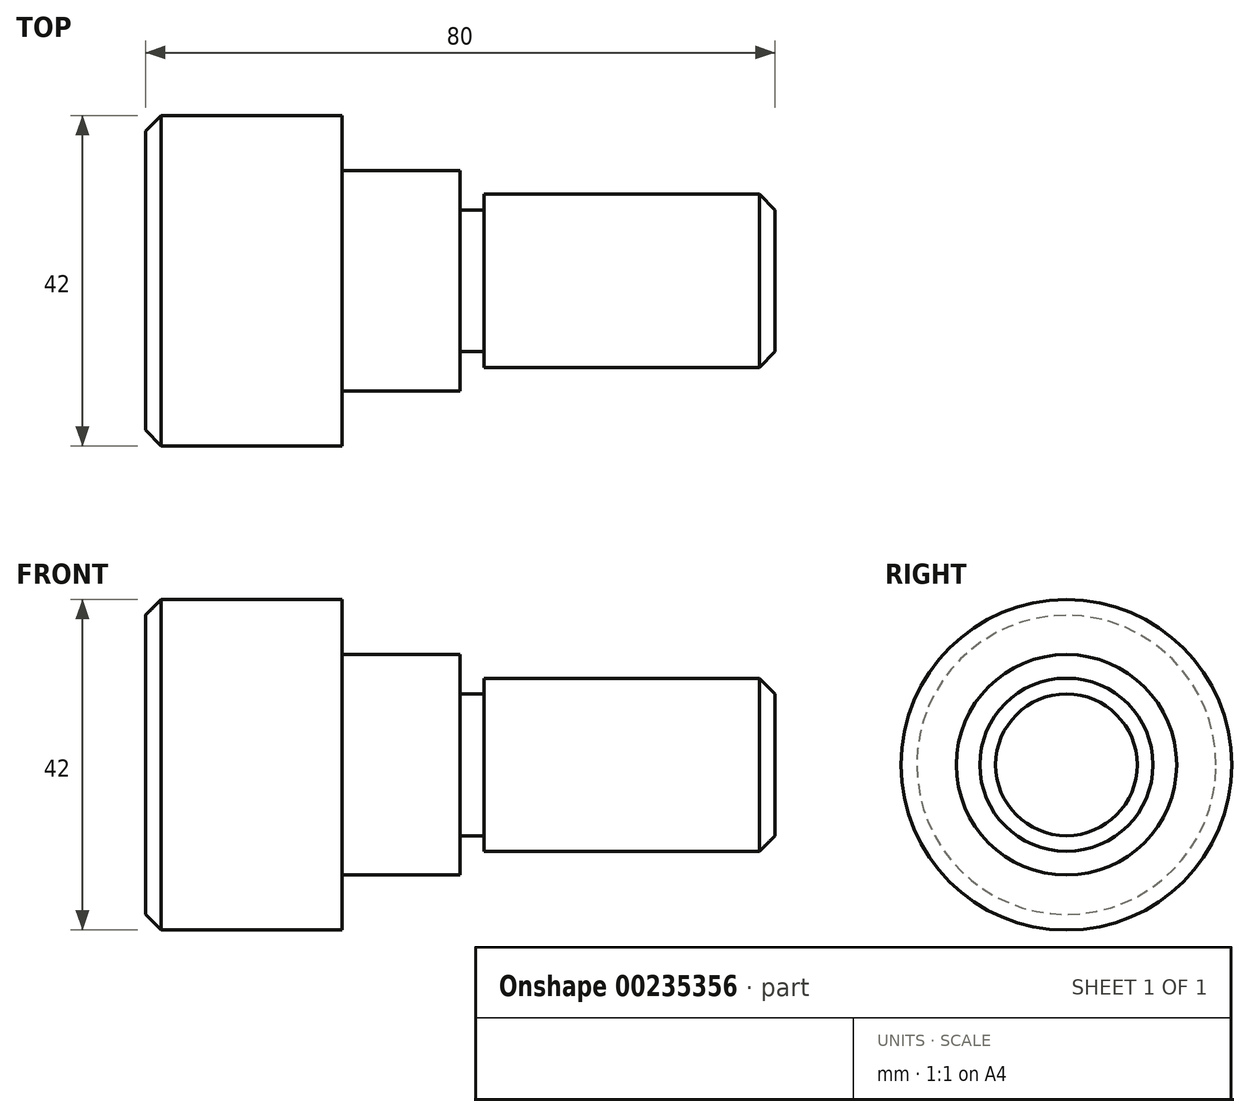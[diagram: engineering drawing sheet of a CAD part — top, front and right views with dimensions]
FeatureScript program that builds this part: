
annotation { "Feature Type Name" : "Feature", "Feature Type Description" : "" }
export const myFeature = defineFeature(function(context is Context, id is Id, definition is map)
    precondition{}
    {
        {
            var Q0;
            Q0=qCreatedBy(makeId("Top.planeOp"),FACE);
            var sketch = newSketch(context, id + "F0", { "sketchPlane" : qUnion([Q0])});
            skLineSegment(sketch, "E0", {"start": v(0, 0) * mm, "end": v(0, 21) * mm});
            skLineSegment(sketch, "E1", {"start": v(0, 21) * mm, "end": v(25, 21) * mm});
            skLineSegment(sketch, "E2", {"start": v(25, 21) * mm, "end": v(25, 14) * mm});
            skLineSegment(sketch, "E3", {"start": v(25, 14) * mm, "end": v(40, 14) * mm});
            skLineSegment(sketch, "E4", {"start": v(40, 14) * mm, "end": v(40, 9) * mm});
            skLineSegment(sketch, "E5", {"start": v(40, 9) * mm, "end": v(43, 9) * mm});
            skLineSegment(sketch, "E6", {"start": v(43, 9) * mm, "end": v(43, 11) * mm});
            skLineSegment(sketch, "E7", {"start": v(43, 11) * mm, "end": v(80, 11) * mm});
            skLineSegment(sketch, "E8", {"start": v(80, 11) * mm, "end": v(80, 0) * mm});
            skLineSegment(sketch, "E9", {"start": v(0, 0) * mm, "end": v(80, 0) * mm});
            skSolve(sketch);
        }
        {
            var Q0;
            Q0=makeQuery(id+"F0.imprint","IMPRINT",FACE,{"disambiguationData":[TD([[makeQuery(id+"F0.imprint","IMPRINT",EDGE,{"derivedFrom":sQuery(id+"F0.wireOp",EDGE,"E0")}),-1.0]])]});
            var Q1;
            Q1=sQuery(id+"F0.wireOp",EDGE,"E9");
            revolve(context, id + "F1", {"entities" : qUnion([Q0]), "axis" : qUnion([Q1]), "revolveType" : RevolveType.FULL});
        }
        {
            var Q0;
            Q0=makeQuery(id+"F1.opRevolve","SWEPT_EDGE",EDGE,{"disambiguationData":[OSD([sQuery(id+"F0.wireOp",EDGE,"E7"),sQuery(id+"F0.wireOp",EDGE,"E8")])]});
            var Q1;
            Q1=makeQuery(id+"F1.opRevolve","SWEPT_EDGE",EDGE,{"disambiguationData":[OSD([sQuery(id+"F0.wireOp",EDGE,"E0"),sQuery(id+"F0.wireOp",EDGE,"E1")])]});
            chamfer(context, id + "F2", {"entities" : qUnion([Q0, Q1]), "chamferType" : ChamferType.OFFSET_ANGLE, "width" : 2 * mm, "oppositeDirection" : false, "angle" : 45 * degree, "tangentPropagation" : true});
        }
    });
